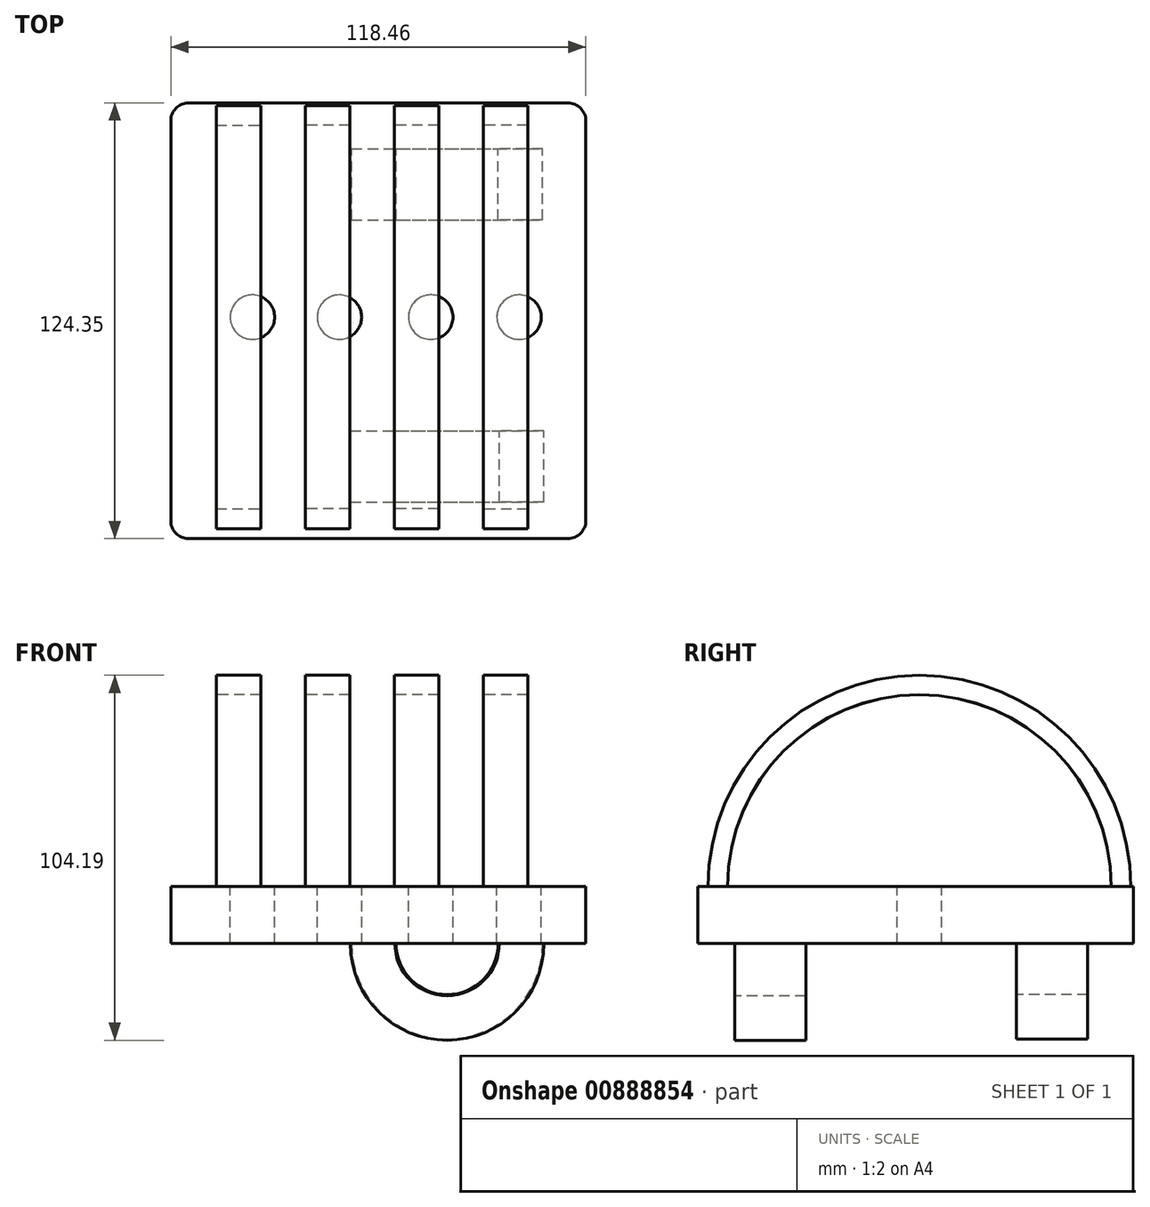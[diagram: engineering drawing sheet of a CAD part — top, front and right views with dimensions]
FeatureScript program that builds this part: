
annotation { "Feature Type Name" : "Feature", "Feature Type Description" : "" }
export const myFeature = defineFeature(function(context is Context, id is Id, definition is map)
    precondition{}
    {
        {
            var Q0;
            Q0=qCreatedBy(makeId("Top.planeOp"),FACE);
            var sketch = newSketch(context, id + "F0", { "sketchPlane" : qUnion([Q0])});
            skLineSegment(sketch, "E0.bottom", {"start": v(53.72, 54.76) * mm, "end": v(41.02, 54.76) * mm});
            skLineSegment(sketch, "E0.top", {"start": v(53.72, 60.34) * mm, "end": v(41.02, 60.34) * mm});
            skLineSegment(sketch, "E0.left", {"start": v(53.72, 54.76) * mm, "end": v(53.72, 60.34) * mm});
            skLineSegment(sketch, "E0.right", {"start": v(41.02, 54.76) * mm, "end": v(41.02, 60.34) * mm});
            skLineSegment(sketch, "E1.bottom", {"start": v(28.32, 60.34) * mm, "end": v(15.62, 60.34) * mm});
            skLineSegment(sketch, "E1.top", {"start": v(28.32, 54.75) * mm, "end": v(15.62, 54.75) * mm});
            skLineSegment(sketch, "E1.left", {"start": v(28.32, 60.34) * mm, "end": v(28.32, 54.75) * mm});
            skLineSegment(sketch, "E1.right", {"start": v(15.62, 60.34) * mm, "end": v(15.62, 54.75) * mm});
            skLineSegment(sketch, "E2.bottom", {"start": v(2.92, 60.34) * mm, "end": v(-9.78, 60.34) * mm});
            skLineSegment(sketch, "E2.top", {"start": v(2.92, 54.75) * mm, "end": v(-9.78, 54.75) * mm});
            skLineSegment(sketch, "E2.left", {"start": v(2.92, 60.34) * mm, "end": v(2.92, 54.75) * mm});
            skLineSegment(sketch, "E2.right", {"start": v(-9.78, 60.34) * mm, "end": v(-9.78, 54.75) * mm});
            skLineSegment(sketch, "E3.bottom", {"start": v(-35.18, 60.34) * mm, "end": v(-22.48, 60.34) * mm});
            skLineSegment(sketch, "E3.top", {"start": v(-35.18, 54.75) * mm, "end": v(-22.48, 54.75) * mm});
            skLineSegment(sketch, "E3.left", {"start": v(-35.18, 60.34) * mm, "end": v(-35.18, 54.75) * mm});
            skLineSegment(sketch, "E3.right", {"start": v(-22.48, 60.34) * mm, "end": v(-22.48, 54.75) * mm});
            skLineSegment(sketch, "E4", {"start": v(-55.68, 0) * mm, "end": v(63.13, 0) * mm});
            skSolve(sketch);
        }
        {
            var Q0;
            Q0 = qSketchRegion(id + "F0", true);
            var Q1;
            Q1=sQuery(id+"F0.wireOp",EDGE,"E4");
            revolve(context, id + "F1", {"surfaceOperationType" : NewSurfaceOperationType.NEW, "entities" : qUnion([Q0]), "axis" : qUnion([Q1]), "revolveType" : RevolveType.ONE_DIRECTION, "angle" : 180 * degree});
        }
        {
            var Q0;
            Q0=qCreatedBy(makeId("Top.planeOp"),FACE);
            var sketch = newSketch(context, id + "F2", { "sketchPlane" : qUnion([Q0])});
            skLineSegment(sketch, "E5.bottom", {"start": v(70.33, -63.21) * mm, "end": v(-48.13, -63.21) * mm});
            skLineSegment(sketch, "E5.top", {"start": v(70.33, 61.14) * mm, "end": v(-48.13, 61.14) * mm});
            skLineSegment(sketch, "E5.left", {"start": v(70.33, -63.21) * mm, "end": v(70.33, 61.14) * mm});
            skLineSegment(sketch, "E5.right", {"start": v(-48.13, -63.21) * mm, "end": v(-48.13, 61.14) * mm});
            skLineSegment(sketch, "E6.bottom", {"start": v(70.33, 22.18) * mm, "end": v(-48.13, 22.18) * mm});
            skLineSegment(sketch, "E6.top", {"start": v(70.33, -18.57) * mm, "end": v(-48.13, -18.57) * mm});
            skLineSegment(sketch, "E6.left", {"start": v(70.33, 22.18) * mm, "end": v(70.33, -18.57) * mm});
            skLineSegment(sketch, "E6.right", {"start": v(-48.13, 22.18) * mm, "end": v(-48.13, -18.57) * mm});
            skCircle(sketch, "E7", {"center": v(51.28, 0) * mm, "radius": 6.35 * mm});
            skCircle(sketch, "E8", {"center": v(26.07, 0) * mm, "radius": 6.35 * mm});
            skCircle(sketch, "E9", {"center": v(0, 0) * mm, "radius": 6.35 * mm});
            skCircle(sketch, "E10", {"center": v(-24.82, 0) * mm, "radius": 6.35 * mm});
            skSolve(sketch);
        }
        {
            var Q0;
            Q0 = qSketchRegion(id + "F2", true);
            extrude(context, id + "F3", {"entities" : qUnion([Q0]), "oppositeDirection" : true, "depth" : 16.26 * mm, "offsetDistance" : 25.4 * mm});
        }
        {
            var Q0;
            Q0=makeQuery(id+"F3.opExtrude","SWEPT_EDGE",EDGE,{"disambiguationData":[OSD([sQuery(id+"F2.wireOp",EDGE,"E5.top"),sQuery(id+"F2.wireOp",EDGE,"E5.right")])]});
            var Q1;
            Q1=makeQuery(id+"F3.opExtrude","SWEPT_EDGE",EDGE,{"disambiguationData":[OSD([sQuery(id+"F2.wireOp",EDGE,"E5.bottom"),sQuery(id+"F2.wireOp",EDGE,"E5.right")])]});
            var Q2;
            Q2=makeQuery(id+"F3.opExtrude","SWEPT_EDGE",EDGE,{"disambiguationData":[OSD([sQuery(id+"F2.wireOp",EDGE,"E5.bottom"),sQuery(id+"F2.wireOp",EDGE,"E5.left")])]});
            var Q3;
            Q3=makeQuery(id+"F3.opExtrude","SWEPT_EDGE",EDGE,{"disambiguationData":[OSD([sQuery(id+"F2.wireOp",EDGE,"E5.top"),sQuery(id+"F2.wireOp",EDGE,"E5.left")])]});
            fillet(context, id + "F4", {"entities" : qUnion([Q0, Q1, Q2, Q3]), "radius" : 5.08 * mm, "tangentPropagation" : true, "allowEdgeOverflow" : false});
        }
        {
            var Q0;
            Q0=makeQuery(id+"F3.opExtrude","CAP_FACE",FACE,{"disambiguationData":[OSD([sQuery(id+"F2.wireOp",EDGE,"E5.bottom"),sQuery(id+"F2.wireOp",EDGE,"E5.top"),sQuery(id+"F2.wireOp",EDGE,"E5.left"),sQuery(id+"F2.wireOp",EDGE,"E5.right"),sQuery(id+"F2.wireOp",EDGE,"E6.left"),sQuery(id+"F2.wireOp",EDGE,"E6.right"),sQuery(id+"F2.wireOp",EDGE,"E7"),sQuery(id+"F2.wireOp",EDGE,"E8"),sQuery(id+"F2.wireOp",EDGE,"E9"),sQuery(id+"F2.wireOp",EDGE,"E10")])],"isStart":false});
            var sketch = newSketch(context, id + "F5", { "sketchPlane" : qUnion([Q0])});
            skLineSegment(sketch, "E11.bottom", {"start": v(58.33, 52.75) * mm, "end": v(45.63, 52.75) * mm});
            skLineSegment(sketch, "E11.top", {"start": v(58.33, 32.43) * mm, "end": v(45.63, 32.43) * mm});
            skLineSegment(sketch, "E11.left", {"start": v(58.33, 52.75) * mm, "end": v(58.33, 32.43) * mm});
            skLineSegment(sketch, "E11.right", {"start": v(45.63, 52.75) * mm, "end": v(45.63, 32.43) * mm});
            skLineSegment(sketch, "E12.bottom", {"start": v(57.99, -27.74) * mm, "end": v(45.29, -27.74) * mm});
            skLineSegment(sketch, "E12.top", {"start": v(57.99, -48.06) * mm, "end": v(45.29, -48.06) * mm});
            skLineSegment(sketch, "E12.left", {"start": v(57.99, -27.74) * mm, "end": v(57.99, -48.06) * mm});
            skLineSegment(sketch, "E12.right", {"start": v(45.29, -27.74) * mm, "end": v(45.29, -48.06) * mm});
            skLineSegment(sketch, "E13", {"start": v(30.73, 63.21) * mm, "end": v(30.73, -61.14) * mm});
            skSolve(sketch);
        }
        {
            var Q0;
            Q0=makeQuery(id+"F5.imprint","IMPRINT",FACE,{"disambiguationData":[TD([[makeQuery(id+"F5.imprint","IMPRINT",EDGE,{"derivedFrom":sQuery(id+"F5.wireOp",EDGE,"E11.bottom")}),1.0]])]});
            var Q1;
            Q1=makeQuery(id+"F5.imprint","IMPRINT",FACE,{"disambiguationData":[TD([[makeQuery(id+"F5.imprint","IMPRINT",EDGE,{"derivedFrom":sQuery(id+"F5.wireOp",EDGE,"E12.bottom")}),1.0]])]});
            var Q2;
            Q2=sQuery(id+"F5.wireOp",EDGE,"E13");
            revolve(context, id + "F6", {"surfaceOperationType" : NewSurfaceOperationType.NEW, "entities" : qUnion([Q0, Q1]), "axis" : qUnion([Q2]), "revolveType" : RevolveType.ONE_DIRECTION, "angle" : 180 * degree});
        }
    });
